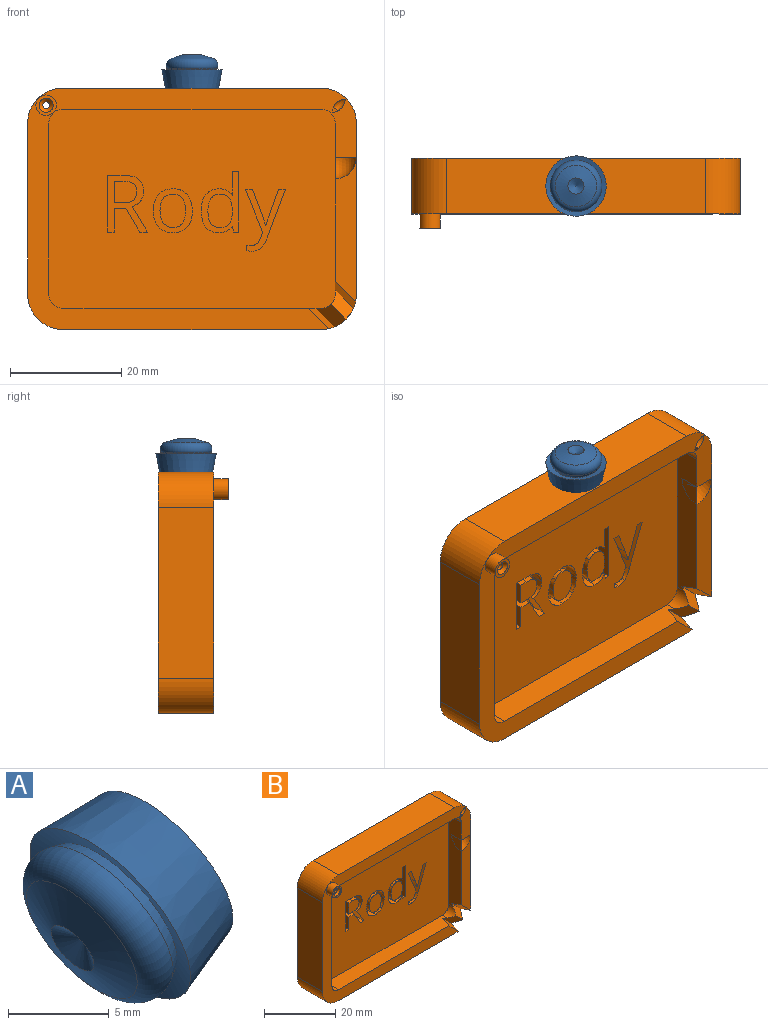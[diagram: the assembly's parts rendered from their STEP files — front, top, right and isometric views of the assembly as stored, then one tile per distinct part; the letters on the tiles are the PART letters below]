
ASSEMBLY  parts=2 mates=1
PART A: 7 faces, bbox 8.2x10.8x10.8 mm
  f0: cone r=4.65mm half-angle=87deg, axis (0.96,0,0.28), area 68.1mm2, adj f1
  f1: cone r=5.42mm half-angle=11deg, axis (-0.96,0,-0.28), area 126.9mm2, adj f0,f2
  f2: cone r=5.42mm half-angle=75deg, axis (-0.96,0,-0.28), area 37.6mm2, adj f1,f3
  f3: cone r=4.52mm half-angle=25.4deg, axis (-0.96,0,-0.28), area 19mm2, adj f2,f4
  f4: torus R=3.37mm, axis (-0.96,0,-0.28), area 60.5mm2, adj f3,f5
  f5: cone r=3.73mm half-angle=73.5deg, axis (0.96,0,0.28), area 38.8mm2, adj f4,f6
  f6: cone r=0mm half-angle=60.2deg, axis (-0.96,0,-0.28), area 7.6mm2, adj f5
PART B: 114 faces, bbox 59.2x12.7x43.5 mm
  f0: plane 59.12x43.45mm, normal (0,-1,0), area 556.9mm2, adj f1,f92,f93,f94,f95,f96,f97,f98
  f1: plane 30.68x5mm, normal (-1,0,0), area 147.9mm2, adj f0,f2,f4,f87,f89,f90,f91,f92
  f2: cylinder r=2.54mm len=3.63mm, axis (0,-1,0), area 10.9mm2, adj f1,f3,f4,f91,f97
  f3: plane 5.64x4.25mm, normal (-0.49,-0.72,-0.49), area 14.4mm2, adj f2,f91,f97,f98,f99
  f4: plane 51.43x35.76mm, normal (0,-1,0), area 1670mm2, adj f1,f2,f5,f7,f8,f9,f10,f11
  f5: extruded ~2.54x1.7mm, area 5.9mm2, adj f4,f6,f7,f21
  f6: plane 11.06x7.16mm, normal (0,-1,0), area 22.6mm2, adj f5,f7,f8,f9,f10,f11,f12,f13
  f7: extruded ~2.54x0.86mm, area 2.2mm2, adj f4,f5,f6,f8
  f8: plane 2.54x0.93mm, normal (1,0,0), area 2.3mm2, adj f4,f6,f7,f9
  f9: extruded ~2.54x1.05mm, area 2.7mm2, adj f4,f6,f8,f10
  f10: extruded ~2.54x1.6mm, area 4.4mm2, adj f4,f6,f9,f11
  f11: extruded ~2.54x1.83mm, area 5.5mm2, adj f4,f6,f10,f12
  f12: plane 8.69x3.28mm, normal (-0.94,0,0.35), area 23.6mm2, adj f4,f6,f11,f13
  f13: plane 2.54x1.24mm, normal (0,0,-1), area 3.1mm2, adj f4,f6,f12,f14
  f14: extruded ~5.29x2.54mm, area 14.3mm2, adj f4,f6,f13,f15
  f15: extruded ~2.54x1.22mm, area 3.2mm2, adj f4,f6,f14,f16
  f16: plane 2.54x0.06mm, normal (0,0,-1), area 0.1mm2, adj f4,f6,f15,f17
  f17: extruded ~2.54x2.15mm, area 5.7mm2, adj f4,f6,f16,f18
  f18: plane 4.35x2.54mm, normal (-0.93,0,-0.36), area 11.8mm2, adj f4,f6,f17,f19
  f19: plane 2.54x1.24mm, normal (0,0,-1), area 3.2mm2, adj f4,f6,f18,f20
  f20: plane 7.68x3.08mm, normal (0.93,0,0.37), area 21mm2, adj f4,f6,f19,f21
  f21: plane 2.54x1.09mm, normal (0.93,0,-0.37), area 3mm2, adj f4,f5,f6,f20
  f22: plane 2.54x1.4mm, normal (0,0,1), area 3.6mm2, adj f4,f23,f32,f41
  f23: plane 10.18x7.17mm, normal (0,-1,0), area 31.1mm2, adj f22,f24,f26,f27,f28,f29,f30,f31
  f24: plane 2.54x1.63mm, normal (0,0,-1), area 4.1mm2, adj f23,f25,f26,f31
  f25: plane 4.05x3.89mm, normal (0,-1,0), area 14.2mm2, adj f24,f26,f27,f28,f29,f30,f31
  f26: extruded ~2.54x1.84mm, area 4.9mm2, adj f23,f24,f25,f27
  f27: extruded ~2.54x1.49mm, area 4.2mm2, adj f23,f25,f26,f28
  f28: extruded ~2.54x1.46mm, area 4.1mm2, adj f23,f25,f27,f29
  f29: extruded ~2.54x1.91mm, area 5.1mm2, adj f23,f25,f28,f30
  f30: plane 2.54x1.54mm, normal (0,0,1), area 3.9mm2, adj f23,f25,f29,f31
  f31: plane 3.89x2.54mm, normal (-1,0,0), area 9.9mm2, adj f23,f24,f25,f30
  f32: plane 4.58x2.77mm, normal (-0.86,0,-0.52), area 13.6mm2, adj f4,f22,f23,f33
  f33: extruded ~2.73x2.54mm, area 9.4mm2, adj f4,f23,f32,f34
  f34: extruded ~2.54x2.16mm, area 6.2mm2, adj f4,f23,f33,f35
  f35: extruded ~2.77x2.54mm, area 7.4mm2, adj f4,f23,f34,f36
  f36: plane 2.79x2.54mm, normal (0,0,-1), area 7.1mm2, adj f4,f23,f35,f37
  f37: plane 10.18x2.54mm, normal (1,0,0), area 25.9mm2, adj f4,f23,f36,f38
  f38: plane 2.54x1.18mm, normal (0,0,1), area 3mm2, adj f4,f23,f37,f39
  f39: plane 4.24x2.54mm, normal (-1,0,0), area 10.8mm2, adj f4,f23,f38,f40
  f40: plane 2.54x2.13mm, normal (0,0,1), area 5.4mm2, adj f4,f23,f39,f41
  f41: plane 4.24x2.54mm, normal (0.86,0,0.5), area 12.4mm2, adj f4,f22,f23,f40
  f42: extruded ~2.59x2.54mm, area 7.3mm2, adj f4,f43,f53,f60
  f43: plane 7.91x7.01mm, normal (0,-1,0), area 22.4mm2, adj f42,f44,f46,f47,f48,f49,f50,f51
  f44: extruded ~2.54x2.23mm, area 6mm2, adj f43,f45,f46,f52
  f45: plane 5.96x4.62mm, normal (0,-1,0), area 22.8mm2, adj f44,f46,f47,f48,f49,f50,f51,f52
  f46: extruded ~2.54x1.72mm, area 5mm2, adj f43,f44,f45,f47
  f47: extruded ~2.54x1.73mm, area 5mm2, adj f43,f45,f46,f48
  f48: extruded ~2.54x2.23mm, area 6mm2, adj f43,f45,f47,f49
  f49: extruded ~2.54x2.21mm, area 5.9mm2, adj f43,f45,f48,f50
  f50: extruded ~2.54x1.74mm, area 5mm2, adj f43,f45,f49,f51
  f51: extruded ~2.54x1.71mm, area 4.9mm2, adj f43,f45,f50,f52
  f52: extruded ~2.54x2.22mm, area 5.9mm2, adj f43,f44,f45,f51
  f53: extruded ~2.91x2.54mm, area 7.9mm2, adj f4,f42,f43,f54
  f54: extruded ~2.54x2.1mm, area 5.5mm2, adj f4,f43,f53,f55
  f55: extruded ~2.54x1.38mm, area 4.8mm2, adj f4,f43,f54,f56
  f56: extruded ~2.54x1.82mm, area 4.8mm2, adj f4,f43,f55,f57
  f57: extruded ~2.6x2.54mm, area 7.3mm2, adj f4,f43,f56,f58
  f58: extruded ~2.92x2.54mm, area 8mm2, adj f4,f43,f57,f59
  f59: extruded ~2.88x2.54mm, area 7.9mm2, adj f4,f43,f58,f60
  f60: extruded ~2.54x2.54mm, area 7.2mm2, adj f4,f42,f43,f59
  f61: plane 10.84x2.54mm, normal (-1,0,0), area 27.5mm2, adj f4,f62,f73,f86
  f62: plane 10.98x6.72mm, normal (0,-1,0), area 28.4mm2, adj f61,f63,f65,f66,f67,f68,f69,f70
  f63: extruded ~2.54x1.72mm, area 4.8mm2, adj f62,f64,f65,f72
  f64: plane 5.98x4.36mm, normal (0,-1,0), area 21.9mm2, adj f63,f65,f66,f67,f68,f69,f70,f71
  f65: extruded ~2.54x2.08mm, area 5.6mm2, adj f62,f63,f64,f66
  f66: plane 2.54x0.24mm, normal (1,0,0), area 0.6mm2, adj f62,f64,f65,f67
  f67: extruded ~2.54x2.32mm, area 6.1mm2, adj f62,f64,f66,f68
  f68: extruded ~2.54x1.72mm, area 4.9mm2, adj f62,f64,f67,f69
  f69: extruded ~2.54x1.56mm, area 4.6mm2, adj f62,f64,f68,f70
  f70: extruded ~2.54x2.23mm, area 5.9mm2, adj f62,f64,f69,f71
  f71: extruded ~2.54x2.21mm, area 5.9mm2, adj f62,f64,f70,f72
  f72: extruded ~2.54x1.57mm, area 4.6mm2, adj f62,f63,f64,f71
  f73: plane 2.54x1.16mm, normal (0,0,-1), area 2.9mm2, adj f4,f61,f62,f74
  f74: plane 3.11x2.54mm, normal (1,0,0), area 7.9mm2, adj f4,f62,f73,f75
  f75: plane 2.54x0.54mm, normal (1,0,0.05), area 1.4mm2, adj f4,f62,f74,f76
  f76: plane 2.54x0.55mm, normal (1,0,0.09), area 1.4mm2, adj f4,f62,f75,f77
  f77: plane 2.54x0.09mm, normal (0,0,-1), area 0.2mm2, adj f4,f62,f76,f78
  f78: extruded ~2.54x2.38mm, area 7mm2, adj f4,f62,f77,f79
  f79: extruded ~2.54x2.33mm, area 6.7mm2, adj f4,f62,f78,f80
  f80: extruded ~2.93x2.54mm, area 7.9mm2, adj f4,f62,f79,f81
  f81: extruded ~2.91x2.54mm, area 7.8mm2, adj f4,f62,f80,f82
  f82: extruded ~2.54x2.33mm, area 6.7mm2, adj f4,f62,f81,f83
  f83: extruded ~2.54x2.4mm, area 7.1mm2, adj f4,f62,f82,f84
  f84: plane 2.54x0.06mm, normal (0,0,1), area 0.2mm2, adj f4,f62,f83,f85
  f85: plane 2.54x1.02mm, normal (0.99,0,0.15), area 2.6mm2, adj f4,f62,f84,f86
  f86: plane 2.54x0.94mm, normal (0,0,1), area 2.4mm2, adj f4,f61,f62,f85
  f87: cone r=0mm half-angle=89.8deg, axis (1,0,0), area 11.4mm2, adj f1,f88,f111
  f88: sphere r=3.81mm, area 22.7mm2, adj f87,f89,f111
  f89: plane 25.93x3.81mm, normal (0,-1,0), area 80.7mm2, adj f1,f88,f90,f99,f110
  f90: plane 4.85x3.88mm, normal (-0.68,-0.26,-0.68), area 19.4mm2, adj f1,f89,f91,f99
  f91: plane 5.41x4.18mm, normal (0.51,-0.69,0.51), area 13.7mm2, adj f1,f2,f3,f90,f99
  f92: cylinder r=2.54mm len=5mm, axis (0,-1,0), area 19.9mm2, adj f0,f1,f4,f93
  f93: plane 46.35x5mm, normal (0,0,-1), area 231.8mm2, adj f0,f4,f92,f94
  f94: cylinder r=2.54mm len=5mm, axis (0,-1,0), area 19.9mm2, adj f0,f4,f93,f95
  f95: plane 30.68x5mm, normal (1,0,0), area 153.4mm2, adj f0,f4,f94,f96
  f96: cylinder r=2.54mm len=5mm, axis (0,-1,0), area 19.9mm2, adj f0,f4,f95,f97
  f97: plane 46.35x5mm, normal (0,0,1), area 225.8mm2, adj f0,f2,f3,f4,f96,f98
  f98: plane 4.77x3.88mm, normal (0.69,-0.24,0.69), area 19.5mm2, adj f0,f3,f97,f99
  f99: cylinder r=6.35mm len=10mm, axis (0,1,0), area 82.7mm2, adj f0,f3,f89,f90,f91,f98,f100,f104
  f100: plane 59.05x43.38mm, normal (0,1,0), area 2525.5mm2, adj f99,f101,f104,f105,f106,f107,f108,f109
  f101: cylinder r=0.64mm len=11.91mm, axis (0,-1,0), area 47.5mm2, adj f100,f102
  f102: cone r=0.64mm half-angle=45deg, axis (0,-1,0), area 5.4mm2, adj f101,f103
  f103: plane 3.7x3.7mm, normal (0,-1,0), area 5.7mm2, adj f102,f112
  f104: plane 46.35x10mm, normal (0,0,-1), area 463.5mm2, adj f0,f99,f100,f105
  f105: cylinder r=6.35mm len=10mm, axis (0,1,0), area 99.7mm2, adj f0,f100,f104,f106
  f106: plane 30.68x10mm, normal (-1,0,0), area 306.8mm2, adj f0,f100,f105,f107
  f107: cylinder r=6.35mm len=10mm, axis (0,1,0), area 99.7mm2, adj f0,f100,f106,f108
  f108: plane 46.35x10mm, normal (0,0,1), area 463.5mm2, adj f0,f100,f107,f109
  f109: cylinder r=6.35mm len=10mm, axis (0,1,0), area 99.7mm2, adj f0,f100,f108,f110
  f110: plane 30.68x10mm, normal (1,0,0), area 306.8mm2, adj f0,f89,f99,f100,f109
  f111: plane 3.81x3.81mm, normal (0,0,-1), area 11.4mm2, adj f0,f87,f88
  f112: cylinder r=1.85mm len=3.7mm, axis (0,1,0), area 29.5mm2, adj f0,f103
  f113: revolved ~2.38x2.38mm, area 5.2mm2, adj f0
PLACE A rot(axis=(0,1,0),106.5deg) t=(-30.74,8.17,63.36)mm
PLACE B t=(-23.67,8.17,-6.44)mm
MATE parallel A.f1 <-> B.f108  axis (0,0,1) through (-36.79,8.17,21.52)mm
